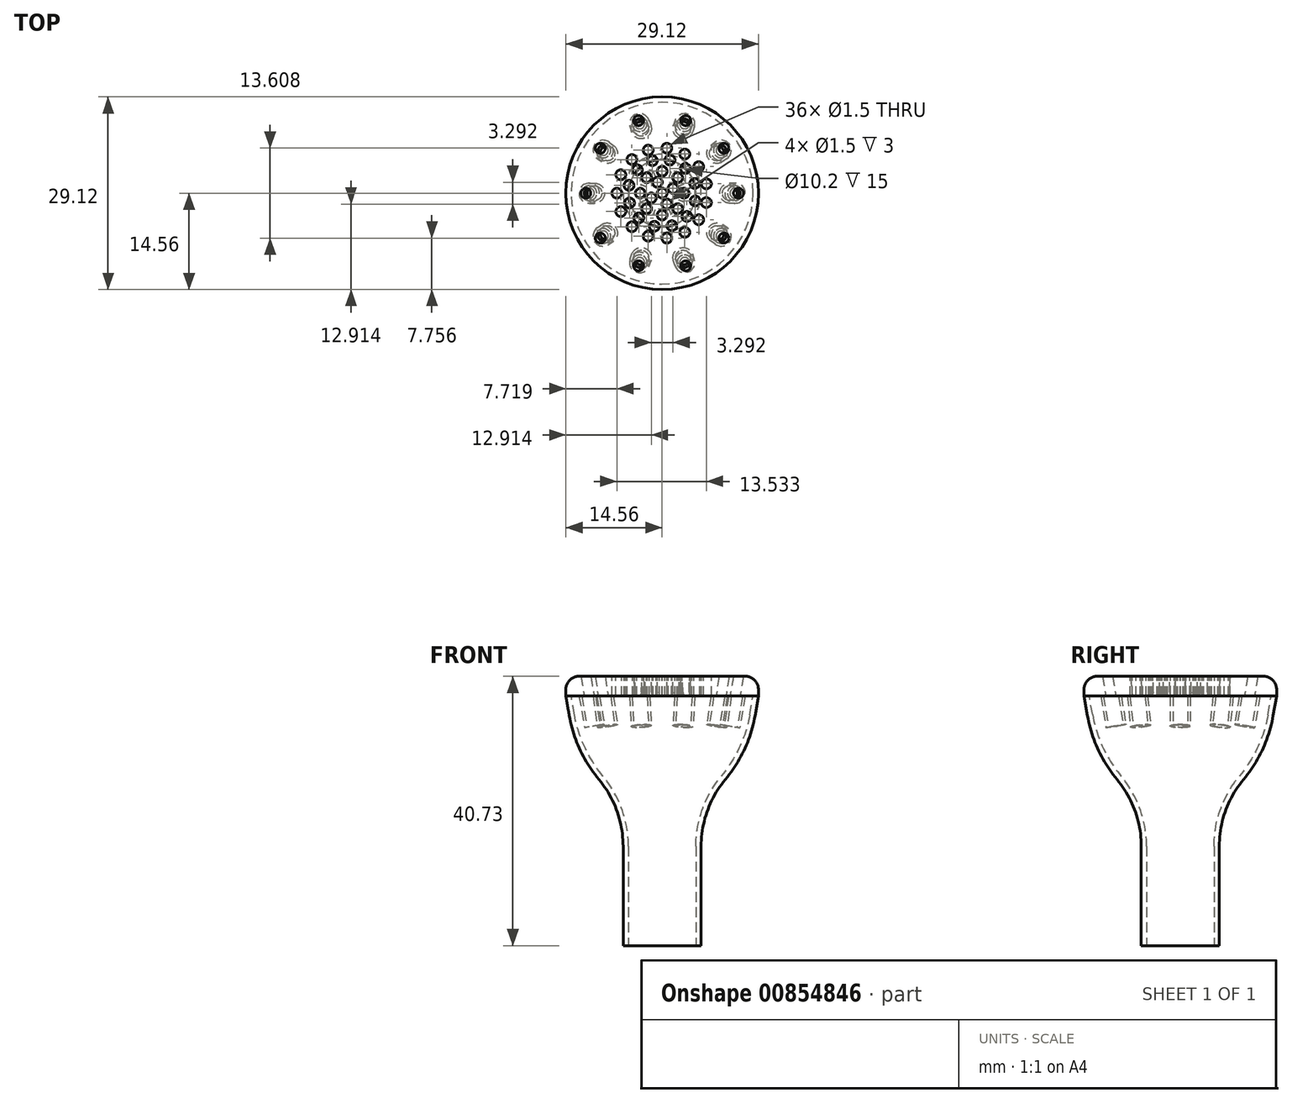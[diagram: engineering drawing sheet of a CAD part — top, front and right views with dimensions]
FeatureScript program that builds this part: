
annotation { "Feature Type Name" : "Feature", "Feature Type Description" : "" }
export const myFeature = defineFeature(function(context is Context, id is Id, definition is map)
    precondition{}
    {
        {
            var Q0;
            Q0=qCreatedBy(makeId("Front.planeOp"),FACE);
            var sketch = newSketch(context, id + "F0", { "sketchPlane" : qUnion([Q0])});
            skArc(sketch, "E0", {"start": v(9.57, 14.4) * mm, "mid": v(6.84, 9.66) * mm, "end": v(5.9, 4.27) * mm});
            skArc(sketch, "E1", {"start": v(9.57, 14.4) * mm, "mid": v(12.43, 18.93) * mm, "end": v(14.04, 24.05) * mm});
            skLineSegment(sketch, "E2", {"start": v(5.9, 4.27) * mm, "end": v(5.9, -10.73) * mm});
            skLineSegment(sketch, "E3", {"start": v(14.56, 30) * mm, "end": v(0, 30) * mm});
            skArc(sketch, "E4", {"start": v(8.95, 14.91) * mm, "mid": v(11.7, 19.27) * mm, "end": v(13.25, 24.18) * mm});
            skArc(sketch, "E5", {"start": v(8.95, 14.91) * mm, "mid": v(6.1, 9.93) * mm, "end": v(5.1, 4.27) * mm});
            skLineSegment(sketch, "E6", {"start": v(5.1, 4.27) * mm, "end": v(5.1, -10.73) * mm});
            skPoint(sketch, "E7.endSnap0", {"position": v(14.56, 27) * mm});
            skLineSegment(sketch, "E8", {"start": v(13.75, 27) * mm, "end": v(0, 27) * mm});
            skLineSegment(sketch, "E9", {"start": v(0, 27) * mm, "end": v(0, 30) * mm});
            skLineSegment(sketch, "E10", {"start": v(5.9, -10.73) * mm, "end": v(5.1, -10.73) * mm});
            skLineSegment(sketch, "E11", {"start": v(14.56, 27) * mm, "end": v(14.56, 30) * mm});
            skLineSegment(sketch, "E12", {"start": v(14.56, 27) * mm, "end": v(14.04, 24.05) * mm});
            skLineSegment(sketch, "E13", {"start": v(13.75, 27) * mm, "end": v(13.25, 24.18) * mm});
            skSolve(sketch);
        }
        {
            var Q0;
            Q0=qSketchRegion(id+"F0",true);
            var Q1;
            Q1=sQuery(id+"F0.wireOp",EDGE,"E9");
            revolve(context, id + "F1", {"surfaceOperationType" : NewSurfaceOperationType.NEW, "entities" : qUnion([Q0]), "axis" : qUnion([Q1]), "revolveType" : RevolveType.FULL});
        }
        {
            var Q0;
            Q0=makeQuery(id+"F1.opRevolve","SWEPT_EDGE",EDGE,{"disambiguationData":[OSD([sQuery(id+"F0.wireOp",EDGE,"E3"),sQuery(id+"F0.wireOp",EDGE,"E11")])]});
            fillet(context, id + "F2", {"entities" : qUnion([Q0]), "radius" : 2 * mm, "tangentPropagation" : true, "allowEdgeOverflow" : false});
        }
        {
            var Q0;
            Q0=qCreatedBy(makeId("Top.planeOp"),FACE);
            var sketch = newSketch(context, id + "F3", { "sketchPlane" : qUnion([Q0])});
            skLineSegment(sketch, "E14.bottom", {"start": v(-45.26, 0) * mm, "end": v(43.56, 0) * mm});
            skLineSegment(sketch, "E14.top", {"start": v(-45.26, -22.33) * mm, "end": v(43.56, -22.33) * mm});
            skLineSegment(sketch, "E14.left", {"start": v(-45.26, 0) * mm, "end": v(-45.26, -22.33) * mm});
            skLineSegment(sketch, "E14.right", {"start": v(43.56, 0) * mm, "end": v(43.56, -22.33) * mm});
            skSolve(sketch);
        }
        {
            var Q0;
            Q0=qCreatedBy(makeId("Front.planeOp"),FACE);
            var sketch = newSketch(context, id + "F4", { "sketchPlane" : qUnion([Q0])});
            skLineSegment(sketch, "E15", {"start": v(11.57, 30.13) * mm, "end": v(10.88, 26.2) * mm});
            skLineSegment(sketch, "E16", {"start": v(11.57, 30.13) * mm, "end": v(12.31, 30) * mm});
            skLineSegment(sketch, "E17", {"start": v(12.31, 30) * mm, "end": v(12.14, 29.02) * mm});
            skLineSegment(sketch, "E18", {"start": v(10.88, 26.2) * mm, "end": v(11.62, 26.06) * mm});
            skLineSegment(sketch, "E19", {"start": v(12.14, 29.02) * mm, "end": v(11.62, 26.06) * mm});
            skSolve(sketch);
        }
        {
            var Q0;
            Q0=qSketchRegion(id+"F4",true);
            var Q1;
            Q1=sQuery(id+"F4.wireOp",EDGE,"E15");
            revolve(context, id + "F5", {"surfaceOperationType" : NewSurfaceOperationType.NEW, "entities" : qUnion([Q0]), "axis" : qUnion([Q1]), "revolveType" : RevolveType.FULL, "oppositeDirection" : true});
        }
        {
            var Q0;
            Q0=makeQuery(id+"F5.opRevolve","SWEPT_BODY",BODY,{"disambiguationData":[OSD([sQuery(id+"F4.wireOp",EDGE,"E15"),sQuery(id+"F4.wireOp",EDGE,"E16"),sQuery(id+"F4.wireOp",EDGE,"E17"),sQuery(id+"F4.wireOp",EDGE,"OWfIclx5-vayt-gKKz-4EJM-t9FRTAjfPkaa"),sQuery(id+"F4.wireOp",EDGE,"E18"),sQuery(id+"F4.wireOp",EDGE,"Z38MXSw5-Bjfm-67RE-bAtL-i3LxWiNijIw8")])]});
            var Q1;
            Q1=makeQuery(id+"F1.opRevolve","SWEPT_FACE",FACE,{"disambiguationData":[OSD([sQuery(id+"F0.wireOp",EDGE,"E11")])]});
            circularPattern(context, id + "F6", {"operationType" : NewBodyOperationType.REMOVE, "entities" : qUnion([Q0]), "axis" : qUnion([Q1]), "angle" : 360 * degree, "instanceCount" : 10, "equalSpace" : true});
        }
        {
            var Q0;
            Q0=qCreatedBy(makeId("Front.planeOp"),FACE);
            var sketch = newSketch(context, id + "F7", { "sketchPlane" : qUnion([Q0])});
            skLineSegment(sketch, "E20.bottom", {"start": v(-18.6, 23.41) * mm, "end": v(25.09, 23.41) * mm});
            skLineSegment(sketch, "E20.top", {"start": v(-18.6, -10.79) * mm, "end": v(25.09, -10.79) * mm});
            skLineSegment(sketch, "E20.left", {"start": v(-18.6, 23.41) * mm, "end": v(-18.6, -10.79) * mm});
            skLineSegment(sketch, "E20.right", {"start": v(25.09, 23.41) * mm, "end": v(25.09, -10.79) * mm});
            skSolve(sketch);
        }
        {
            var Q0;
            Q0=qCreatedBy(makeId("Front.planeOp"),FACE);
            var sketch = newSketch(context, id + "F8", { "sketchPlane" : qUnion([Q0])});
            skLineSegment(sketch, "E21", {"start": v(3.25, 33.02) * mm, "end": v(3.45, 23) * mm});
            skLineSegment(sketch, "E22", {"start": v(3.25, 33.02) * mm, "end": v(2.5, 33) * mm});
            skLineSegment(sketch, "E23", {"start": v(2.7, 23) * mm, "end": v(2.5, 33) * mm});
            skLineSegment(sketch, "E24", {"start": v(2.7, 23) * mm, "end": v(3.45, 23) * mm});
            skSolve(sketch);
        }
        {
            var Q0;
            Q0=makeQuery(id+"F8.imprint","IMPRINT",FACE,{"disambiguationData":[TD([[makeQuery(id+"F8.imprint","IMPRINT",EDGE,{"derivedFrom":sQuery(id+"F8.wireOp",EDGE,"E21")}),-1.0]])]});
            var Q1;
            Q1=sQuery(id+"F8.wireOp",EDGE,"E21");
            revolve(context, id + "F9", {"surfaceOperationType" : NewSurfaceOperationType.NEW, "entities" : qUnion([Q0]), "axis" : qUnion([Q1]), "revolveType" : RevolveType.FULL});
        }
        {
            var Q0;
            Q0=makeQuery(id+"F9.opRevolve","SWEPT_BODY",BODY,{"disambiguationData":[OSD([sQuery(id+"F8.wireOp",EDGE,"E21"),sQuery(id+"F8.wireOp",EDGE,"E22"),sQuery(id+"F8.wireOp",EDGE,"E23"),sQuery(id+"F8.wireOp",EDGE,"E24")])]});
            var Q1;
            Q1=makeQuery(id+"F1.opRevolve","SWEPT_FACE",FACE,{"disambiguationData":[OSD([sQuery(id+"F0.wireOp",EDGE,"E11")])]});
            circularPattern(context, id + "F10", {"operationType" : NewBodyOperationType.REMOVE, "entities" : qUnion([Q0]), "axis" : qUnion([Q1]), "angle" : 360 * degree, "instanceCount" : 8, "equalSpace" : true});
        }
        {
            var Q0;
            Q0=makeQuery(id+"F10.boolean.opBoolean","INTERSECT",EDGE,{"derivedFrom":[makeQuery(id+"F1.opRevolve","SWEPT_FACE",FACE,{"disambiguationData":[OSD([sQuery(id+"F0.wireOp",EDGE,"E8")])]}),makeQuery(id+"F10.opPattern","COPY",FACE,{"derivedFrom":makeQuery(id+"F9.opRevolve","SWEPT_FACE",FACE,{"disambiguationData":[OSD([sQuery(id+"F8.wireOp",EDGE,"E23")])]}),"instanceName":"1"})]});
            var Q1;
            Q1=makeQuery(id+"F10.boolean.opBoolean","INTERSECT",EDGE,{"derivedFrom":[makeQuery(id+"F1.opRevolve","SWEPT_FACE",FACE,{"disambiguationData":[OSD([sQuery(id+"F0.wireOp",EDGE,"E8")])]}),makeQuery(id+"F9.opRevolve","SWEPT_FACE",FACE,{"disambiguationData":[OSD([sQuery(id+"F8.wireOp",EDGE,"E23")])]})]});
            var Q2;
            Q2=makeQuery(id+"F10.boolean.opBoolean","INTERSECT",EDGE,{"derivedFrom":[makeQuery(id+"F1.opRevolve","SWEPT_FACE",FACE,{"disambiguationData":[OSD([sQuery(id+"F0.wireOp",EDGE,"E8")])]}),makeQuery(id+"F10.opPattern","COPY",FACE,{"derivedFrom":makeQuery(id+"F9.opRevolve","SWEPT_FACE",FACE,{"disambiguationData":[OSD([sQuery(id+"F8.wireOp",EDGE,"E23")])]}),"instanceName":"7"})]});
            var Q3;
            Q3=makeQuery(id+"F10.boolean.opBoolean","INTERSECT",EDGE,{"derivedFrom":[makeQuery(id+"F1.opRevolve","SWEPT_FACE",FACE,{"disambiguationData":[OSD([sQuery(id+"F0.wireOp",EDGE,"E8")])]}),makeQuery(id+"F10.opPattern","COPY",FACE,{"derivedFrom":makeQuery(id+"F9.opRevolve","SWEPT_FACE",FACE,{"disambiguationData":[OSD([sQuery(id+"F8.wireOp",EDGE,"E23")])]}),"instanceName":"6"})]});
            var Q4;
            Q4=makeQuery(id+"F10.boolean.opBoolean","INTERSECT",EDGE,{"derivedFrom":[makeQuery(id+"F1.opRevolve","SWEPT_FACE",FACE,{"disambiguationData":[OSD([sQuery(id+"F0.wireOp",EDGE,"E8")])]}),makeQuery(id+"F10.opPattern","COPY",FACE,{"derivedFrom":makeQuery(id+"F9.opRevolve","SWEPT_FACE",FACE,{"disambiguationData":[OSD([sQuery(id+"F8.wireOp",EDGE,"E23")])]}),"instanceName":"5"})]});
            var Q5;
            Q5=makeQuery(id+"F10.boolean.opBoolean","INTERSECT",EDGE,{"derivedFrom":[makeQuery(id+"F1.opRevolve","SWEPT_FACE",FACE,{"disambiguationData":[OSD([sQuery(id+"F0.wireOp",EDGE,"E8")])]}),makeQuery(id+"F10.opPattern","COPY",FACE,{"derivedFrom":makeQuery(id+"F9.opRevolve","SWEPT_FACE",FACE,{"disambiguationData":[OSD([sQuery(id+"F8.wireOp",EDGE,"E23")])]}),"instanceName":"4"})]});
            var Q6;
            Q6=makeQuery(id+"F10.boolean.opBoolean","INTERSECT",EDGE,{"derivedFrom":[makeQuery(id+"F1.opRevolve","SWEPT_FACE",FACE,{"disambiguationData":[OSD([sQuery(id+"F0.wireOp",EDGE,"E8")])]}),makeQuery(id+"F10.opPattern","COPY",FACE,{"derivedFrom":makeQuery(id+"F9.opRevolve","SWEPT_FACE",FACE,{"disambiguationData":[OSD([sQuery(id+"F8.wireOp",EDGE,"E23")])]}),"instanceName":"3"})]});
            var Q7;
            Q7=makeQuery(id+"F10.boolean.opBoolean","INTERSECT",EDGE,{"derivedFrom":[makeQuery(id+"F1.opRevolve","SWEPT_FACE",FACE,{"disambiguationData":[OSD([sQuery(id+"F0.wireOp",EDGE,"E8")])]}),makeQuery(id+"F10.opPattern","COPY",FACE,{"derivedFrom":makeQuery(id+"F9.opRevolve","SWEPT_FACE",FACE,{"disambiguationData":[OSD([sQuery(id+"F8.wireOp",EDGE,"E23")])]}),"instanceName":"2"})]});
            fillet(context, id + "F11", {"entities" : qUnion([Q0, Q1, Q2, Q3, Q4, Q5, Q6, Q7]), "radius" : 0.6 * mm, "tangentPropagation" : true, "allowEdgeOverflow" : false});
        }
        {
            var Q0;
            Q0=makeQuery(id+"F1.opRevolve","SWEPT_FACE",FACE,{"disambiguationData":[OSD([sQuery(id+"F0.wireOp",EDGE,"E3")])]});
            var sketch = newSketch(context, id + "F12", { "sketchPlane" : qUnion([Q0])});
            skCircle(sketch, "E25", {"center": v(-0.72, 1.65) * mm, "radius": 0.75 * mm});
            skCircle(sketch, "E26.1.0", {"center": v(-1.65, -0.72) * mm, "radius": 0.75 * mm});
            skCircle(sketch, "E26.2.0", {"center": v(0.72, -1.65) * mm, "radius": 0.75 * mm});
            skCircle(sketch, "E26.3.0", {"center": v(1.65, 0.72) * mm, "radius": 0.75 * mm});
            skPoint(sketch, "E26.center", {"position": v(0, 0) * mm});
            skCircle(sketch, "E27", {"center": v(0, 0) * mm, "radius": 0.75 * mm});
            skCircle(sketch, "E28", {"center": v(-1.18, -5) * mm, "radius": 0.75 * mm});
            skCircle(sketch, "E29.1.0", {"center": v(1.48, -4.92) * mm, "radius": 0.75 * mm});
            skCircle(sketch, "E29.2.0", {"center": v(3.74, -3.52) * mm, "radius": 0.75 * mm});
            skCircle(sketch, "E29.3.0", {"center": v(5, -1.18) * mm, "radius": 0.75 * mm});
            skCircle(sketch, "E29.4.0", {"center": v(4.92, 1.48) * mm, "radius": 0.75 * mm});
            skCircle(sketch, "E29.5.0", {"center": v(3.52, 3.74) * mm, "radius": 0.75 * mm});
            skCircle(sketch, "E29.6.0", {"center": v(1.18, 5) * mm, "radius": 0.75 * mm});
            skCircle(sketch, "E29.7.0", {"center": v(-1.48, 4.92) * mm, "radius": 0.75 * mm});
            skCircle(sketch, "E29.8.0", {"center": v(-3.74, 3.52) * mm, "radius": 0.75 * mm});
            skCircle(sketch, "E29.9.0", {"center": v(-5, 1.18) * mm, "radius": 0.75 * mm});
            skCircle(sketch, "E29.10.0", {"center": v(-4.92, -1.48) * mm, "radius": 0.75 * mm});
            skCircle(sketch, "E29.11.0", {"center": v(-3.52, -3.74) * mm, "radius": 0.75 * mm});
            skCircle(sketch, "E30", {"center": v(-6.84, 0) * mm, "radius": 0.75 * mm});
            skCircle(sketch, "E31.1.0", {"center": v(-6.25, -2.78) * mm, "radius": 0.75 * mm});
            skCircle(sketch, "E31.2.0", {"center": v(-4.58, -5.08) * mm, "radius": 0.75 * mm});
            skCircle(sketch, "E31.3.0", {"center": v(-2.11, -6.5) * mm, "radius": 0.75 * mm});
            skCircle(sketch, "E31.4.0", {"center": v(0.72, -6.8) * mm, "radius": 0.75 * mm});
            skCircle(sketch, "E31.5.0", {"center": v(3.42, -5.92) * mm, "radius": 0.75 * mm});
            skCircle(sketch, "E31.6.0", {"center": v(5.53, -4.02) * mm, "radius": 0.75 * mm});
            skCircle(sketch, "E31.7.0", {"center": v(6.7, -1.42) * mm, "radius": 0.75 * mm});
            skCircle(sketch, "E31.8.0", {"center": v(6.7, 1.42) * mm, "radius": 0.75 * mm});
            skCircle(sketch, "E31.9.0", {"center": v(5.53, 4.02) * mm, "radius": 0.75 * mm});
            skCircle(sketch, "E31.10.0", {"center": v(3.42, 5.92) * mm, "radius": 0.75 * mm});
            skCircle(sketch, "E31.11.0", {"center": v(0.72, 6.8) * mm, "radius": 0.75 * mm});
            skCircle(sketch, "E31.12.0", {"center": v(-2.11, 6.5) * mm, "radius": 0.75 * mm});
            skCircle(sketch, "E31.13.0", {"center": v(-4.58, 5.08) * mm, "radius": 0.75 * mm});
            skCircle(sketch, "E31.14.0", {"center": v(-6.25, 2.78) * mm, "radius": 0.75 * mm});
            skSolve(sketch);
        }
        {
            var Q0;
            Q0 = qSketchRegion(id + "F0uOTLiABqPNMQZ_1", true);
            var Q1;
            Q1 = qSketchRegion(id + "F12", true);
            extrude(context, id + "F13", {"entities" : qUnion([Q0, Q1]), "operationType" : NewBodyOperationType.REMOVE, "oppositeDirection" : true, "depth" : 10 * mm, "offsetDistance" : 25 * mm});
        }
        {
            var Q0;
            Q0=makeQuery(id+"F13.boolean.opBoolean","INTERSECT",EDGE,{"derivedFrom":[makeQuery(id+"F1.opRevolve","SWEPT_FACE",FACE,{"disambiguationData":[OSD([sQuery(id+"F0.wireOp",EDGE,"E8")])]}),makeQuery(id+"F13.opExtrude","SWEPT_FACE",FACE,{"disambiguationData":[OSD([sQuery(id+"F12.wireOp",EDGE,"E27")])]})]});
            fillet(context, id + "F14", {"entities" : qUnion([Q0]), "radius" : 0.6 * mm, "tangentPropagation" : true, "allowEdgeOverflow" : false});
        }
        {
            var Q0;
            Q0=qCreatedBy(makeId("Front.planeOp"),FACE);
            var sketch = newSketch(context, id + "F15", { "sketchPlane" : qUnion([Q0])});
            skLineSegment(sketch, "E32", {"start": v(12.2, 27.21) * mm, "end": v(12.6, 27.14) * mm});
            skLineSegment(sketch, "E33", {"start": v(12.2, 27.21) * mm, "end": v(11.33, 22.29) * mm});
            skLineSegment(sketch, "E34", {"start": v(11.73, 22.22) * mm, "end": v(11.33, 22.29) * mm});
            skLineSegment(sketch, "E35", {"start": v(11.73, 22.22) * mm, "end": v(12.6, 27.14) * mm});
            skSolve(sketch);
        }
        {
            var Q0;
            Q0 = qSketchRegion(id + "F15", true);
            var Q1;
            Q1=makeQuery(id+"F6.boolean.opBoolean","COPY",FACE,{"derivedFrom":makeQuery(id+"F5.opRevolve","SWEPT_FACE",FACE,{"disambiguationData":[OSD([sQuery(id+"F4.wireOp",EDGE,"E17"),sQuery(id+"F4.wireOp",EDGE,"E19")])]})});
            revolve(context, id + "F16", {"surfaceOperationType" : NewSurfaceOperationType.NEW, "entities" : qUnion([Q0]), "axis" : qUnion([Q1]), "revolveType" : RevolveType.FULL});
        }
        {
            var Q0;
            Q0=makeQuery(id+"F16.opRevolve","SWEPT_BODY",BODY,{"disambiguationData":[OSD([sQuery(id+"F15.wireOp",EDGE,"E32"),sQuery(id+"F15.wireOp",EDGE,"E33"),sQuery(id+"F15.wireOp",EDGE,"E34"),sQuery(id+"F15.wireOp",EDGE,"E35")])]});
            var Q1;
            Q1=makeQuery(id+"F1.opRevolve","SWEPT_EDGE",EDGE,{"disambiguationData":[OSD([sQuery(id+"F0.wireOp",EDGE,"E11"),sQuery(id+"F0.wireOp",EDGE,"E12")])]});
            circularPattern(context, id + "F17", {"operationType" : NewBodyOperationType.ADD, "entities" : qUnion([Q0]), "axis" : qUnion([Q1]), "angle" : 360 * degree, "instanceCount" : 10, "equalSpace" : true});
        }
    });
